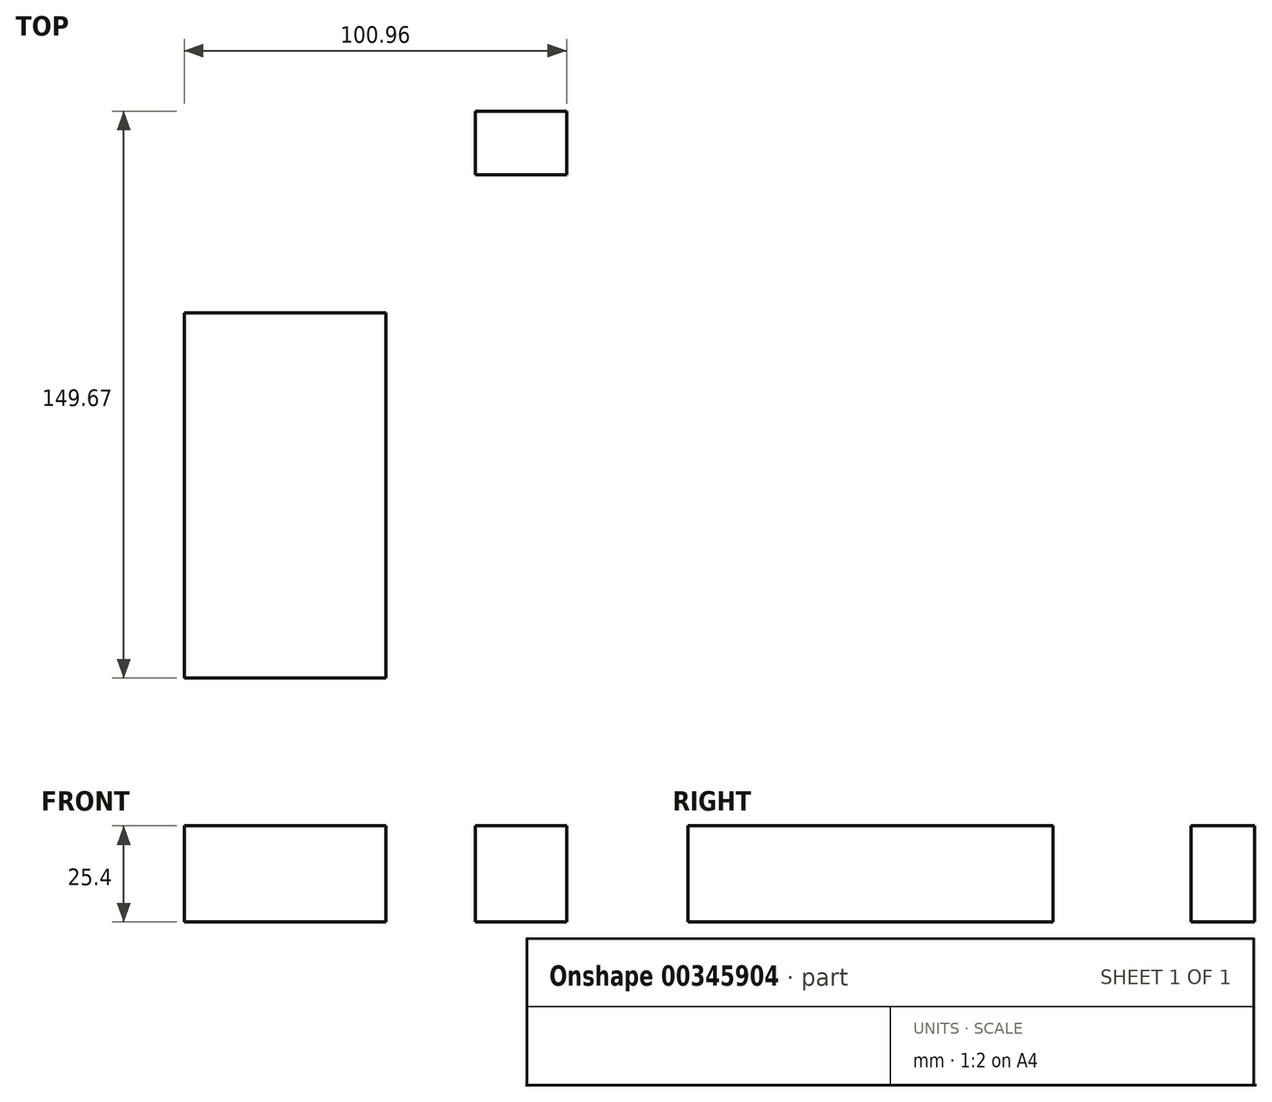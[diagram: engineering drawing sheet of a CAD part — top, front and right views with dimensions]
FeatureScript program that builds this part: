
annotation { "Feature Type Name" : "Feature", "Feature Type Description" : "" }
export const myFeature = defineFeature(function(context is Context, id is Id, definition is map)
    precondition{}
    {
        {
            var Q0;
            Q0=qCreatedBy(makeId("Top.planeOp"),FACE);
            var sketch = newSketch(context, id + "F0", { "sketchPlane" : qUnion([Q0])});
            skLineSegment(sketch, "E0.bottom", {"start": v(-14.22, 56.8) * mm, "end": v(39.07, 56.8) * mm});
            skLineSegment(sketch, "E0.top", {"start": v(-14.22, -39.67) * mm, "end": v(39.07, -39.67) * mm});
            skLineSegment(sketch, "E0.left", {"start": v(-14.22, 56.8) * mm, "end": v(-14.22, -39.67) * mm});
            skLineSegment(sketch, "E0.right", {"start": v(39.07, 56.8) * mm, "end": v(39.07, -39.67) * mm});
            skLineSegment(sketch, "E1.bottom", {"start": v(86.74, 93.2) * mm, "end": v(62.6, 93.2) * mm});
            skLineSegment(sketch, "E1.top", {"start": v(86.74, 110) * mm, "end": v(62.6, 110) * mm});
            skLineSegment(sketch, "E1.left", {"start": v(86.74, 93.2) * mm, "end": v(86.74, 110) * mm});
            skLineSegment(sketch, "E1.right", {"start": v(62.6, 93.2) * mm, "end": v(62.6, 110) * mm});
            skSolve(sketch);
        }
        {
            var Q0;
            Q0 = qSketchRegion(id + "F0", true);
            extrude(context, id + "F1", {"entities" : qUnion([Q0]), "depth" : 25.4 * mm});
        }
    });
